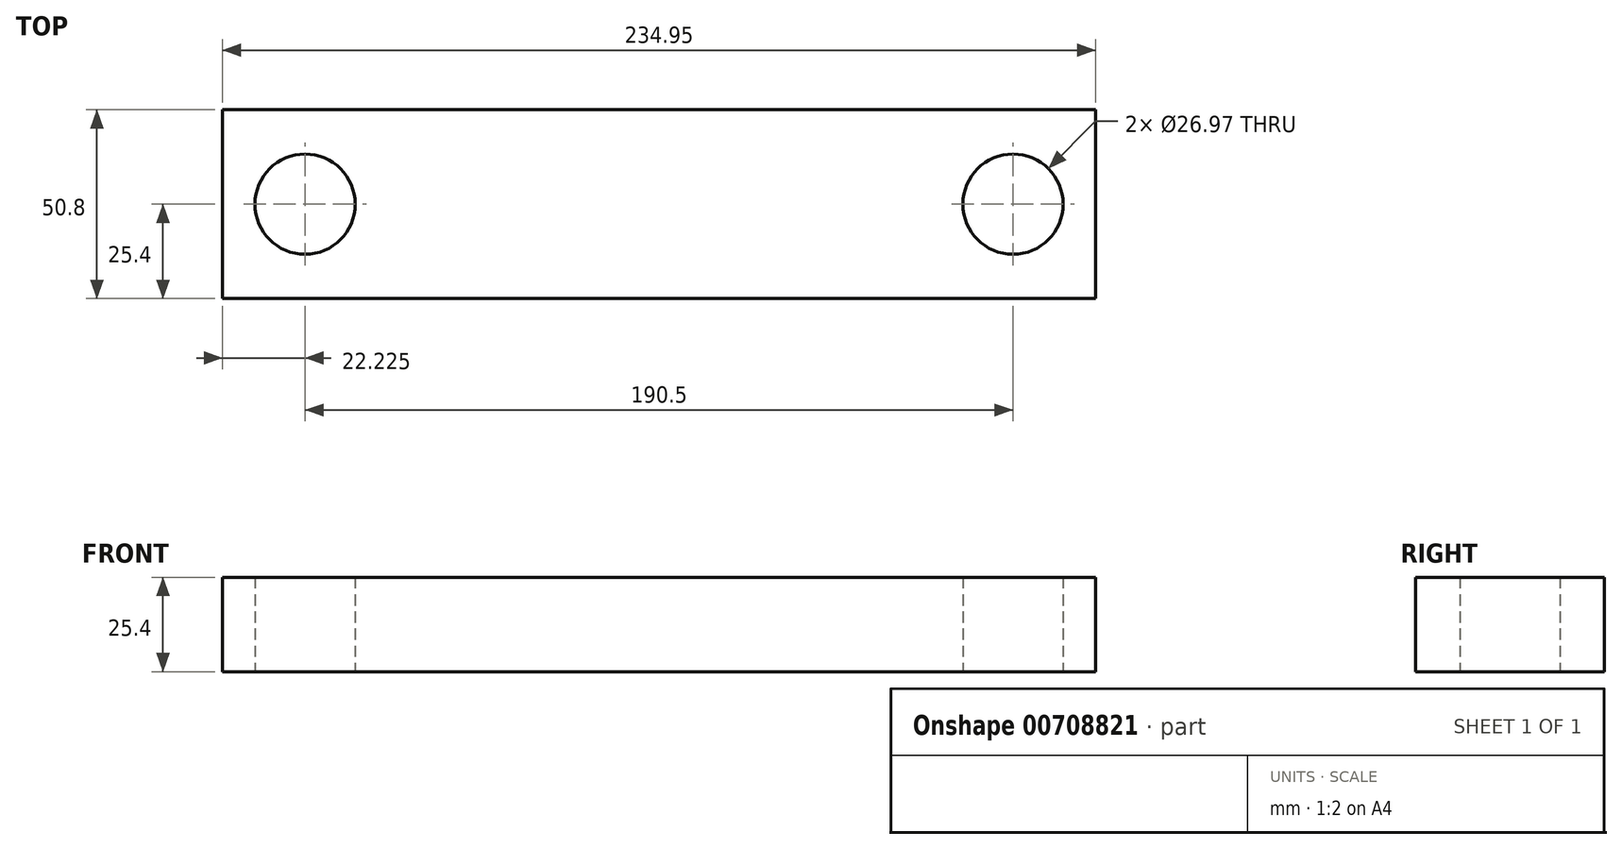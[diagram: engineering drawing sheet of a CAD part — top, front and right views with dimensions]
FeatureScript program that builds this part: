
annotation { "Feature Type Name" : "Feature", "Feature Type Description" : "" }
export const myFeature = defineFeature(function(context is Context, id is Id, definition is map)
    precondition{}
    {
        {
            var Q0;
            Q0=qCreatedBy(makeId("Top.planeOp"),FACE);
            var sketch = newSketch(context, id + "F0", { "sketchPlane" : qUnion([Q0])});
            skLineSegment(sketch, "E0.bottom", {"start": v(0, 0) * mm, "end": v(234.95, 0) * mm});
            skLineSegment(sketch, "E0.top", {"start": v(0, 50.8) * mm, "end": v(234.95, 50.8) * mm});
            skLineSegment(sketch, "E0.left", {"start": v(0, 0) * mm, "end": v(0, 50.8) * mm});
            skLineSegment(sketch, "E0.right", {"start": v(234.95, 0) * mm, "end": v(234.95, 50.8) * mm});
            skLineSegment(sketch, "E1", {"start": v(0, 25.4) * mm, "end": v(35.71, 25.4) * mm, "construction": true});
            skCircle(sketch, "E2", {"center": v(22.23, 25.4) * mm, "radius": 13.49 * mm});
            skCircle(sketch, "E3", {"center": v(212.73, 25.4) * mm, "radius": 13.49 * mm});
            skLineSegment(sketch, "E4.trimOffspring", {"start": v(199.24, 25.4) * mm, "end": v(234.95, 25.4) * mm, "construction": true});
            skSolve(sketch);
        }
        {
            var Q0;
            Q0 = qSketchRegion(id + "F0", true);
            extrude(context, id + "F1", {"entities" : qUnion([Q0]), "depth" : 25.4 * mm, "offsetDistance" : 25.4 * mm});
        }
    });
